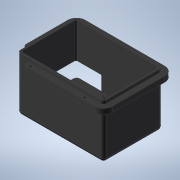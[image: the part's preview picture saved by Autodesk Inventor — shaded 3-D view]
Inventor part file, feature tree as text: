
AUTODESK INVENTOR PART (.ipt)
format: ipt  version: 2021 (Build 250183000, 183)  size: 303,616 bytes
history: native  units: mm
features: sketch x8, other x4, plane x1
ambient origin geometry x8: Origin, YZ Plane, XZ Plane, XY Plane, X Axis, Y Axis, Z Axis, Center Point
bodies: Body1 (feature_tree)
feature tree (13):
  other  "麥克風崁座.ipt"
  other  "實體1::麥克風崁座.ipt"
  other  "標籤特徵1"
  sketch  "草圖1"
  sketch  "草圖2"
  sketch  "草圖3"
  sketch  "草圖7"
  sketch  "草圖8"
  sketch  "草圖9"
  sketch  "草圖10"
  sketch  "草圖11"
  plane  "工作平面1"
  other  "實體1"
